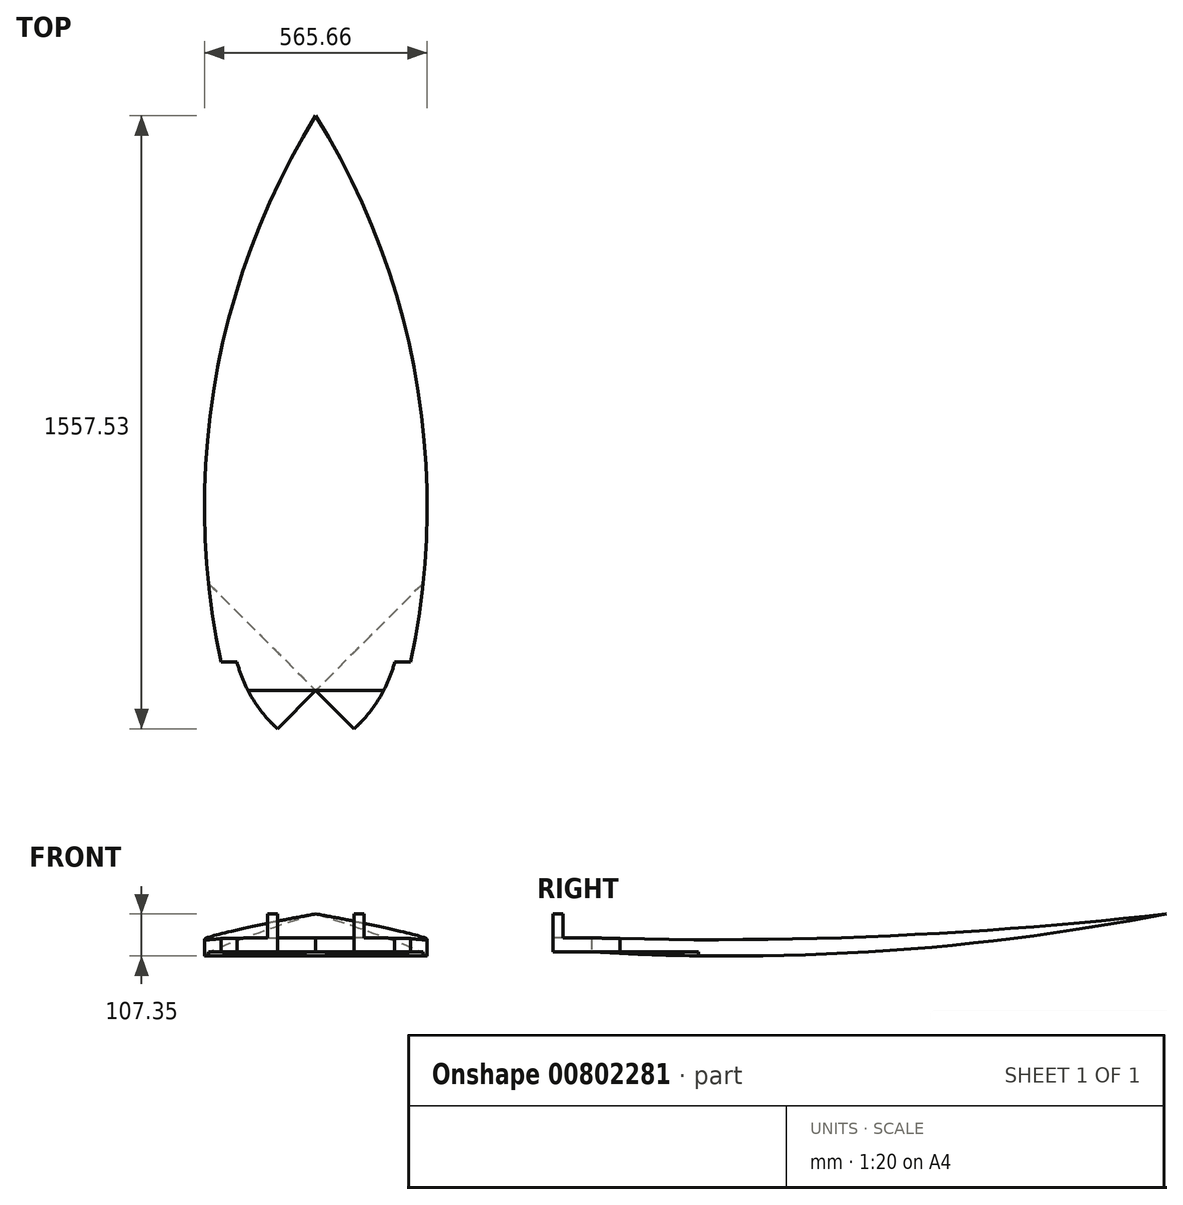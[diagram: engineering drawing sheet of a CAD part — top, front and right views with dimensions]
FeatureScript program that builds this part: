
annotation { "Feature Type Name" : "Feature", "Feature Type Description" : "" }
export const myFeature = defineFeature(function(context is Context, id is Id, definition is map)
    precondition{}
    {
        {
            var Q0;
            Q0=qCreatedBy(makeId("Top.planeOp"),FACE);
            var sketch = newSketch(context, id + "F0", { "sketchPlane" : qUnion([Q0])});
            skLineSegment(sketch, "E0", {"start": v(0, 97.23) * mm, "end": v(0, 1557.53) * mm});
            skArc(sketch, "E1", {"start": v(240.8, 169.76) * mm, "mid": v(255.12, 887.02) * mm, "end": v(0, 1557.53) * mm});
            skLineSegment(sketch, "E2", {"start": v(240.8, 169.76) * mm, "end": v(200.23, 169.76) * mm});
            skArc(sketch, "E3", {"start": v(97.15, 0) * mm, "mid": v(161.15, 77.32) * mm, "end": v(200.23, 169.76) * mm});
            skLineSegment(sketch, "E4", {"start": v(97.15, 0) * mm, "end": v(0, 97.23) * mm});
            skSolve(sketch);
        }
        {
            var Q0;
            Q0=makeQuery(id+"F0.imprint","IMPRINT",FACE,{"disambiguationData":[TD([[makeQuery(id+"F0.imprint","IMPRINT",EDGE,{"derivedFrom":sQuery(id+"F0.wireOp",EDGE,"E0")}),-1.0]])]});
            extrude(context, id + "F1", {"entities" : qUnion([Q0]), "depth" : 121.92 * mm, "offsetDistance" : 30.48 * mm});
        }
        {
            var Q0;
            Q0=makeQuery(id+"F1.opExtrude","SWEPT_FACE",FACE,{"disambiguationData":[OSD([sQuery(id+"F0.wireOp",EDGE,"E0")])]});
            var sketch = newSketch(context, id + "F2", { "sketchPlane" : qUnion([Q0])});
            skArc(sketch, "E5", {"start": v(-1557.53, 121.92) * mm, "mid": v(-828.48, 64.93) * mm, "end": v(-97.23, 60.96) * mm});
            skArc(sketch, "E6", {"start": v(-1557.53, 121.92) * mm, "mid": v(-830.46, 27.02) * mm, "end": v(-97.23, 25.6) * mm});
            skSolve(sketch);
        }
        {
            var Q0;
            {var subQ0=sQuery(id+"F2.wireOp",EDGE,"E5");Q0=makeQuery(id+"F2.imprint","IMPRINT",FACE,{"disambiguationData":[TD([[makeQuery(id+"F2.imprint","IMPRINT",EDGE,{"derivedFrom":subQ0}),1.0]])]});}
            var Q1;
            {var subQ0=sQuery(id+"F2.wireOp",EDGE,"E6");Q1=makeQuery(id+"F2.imprint","IMPRINT",FACE,{"disambiguationData":[TD([[makeQuery(id+"F2.imprint","IMPRINT",EDGE,{"derivedFrom":subQ0}),-1.0]])]});}
            extrude(context, id + "F3", {"entities" : qUnion([Q0, Q1]), "operationType" : NewBodyOperationType.REMOVE, "endBound" : BoundingType.THROUGH_ALL, "oppositeDirection" : true, "depth" : 30.48 * mm, "offsetDistance" : 30.48 * mm});
        }
        {
            var Q0;
            Q0=makeQuery(id+"F1.opExtrude","SWEPT_FACE",FACE,{"disambiguationData":[OSD([sQuery(id+"F0.wireOp",EDGE,"E4")])]});
            var sketch = newSketch(context, id + "F4", { "sketchPlane" : qUnion([Q0])});
            skLineSegment(sketch, "E7", {"start": v(-68.77, 60.96) * mm, "end": v(68.67, 60.96) * mm});
            skLineSegment(sketch, "E8", {"start": v(-68.77, 25.6) * mm, "end": v(68.67, 25.6) * mm});
            skSolve(sketch);
        }
        {
            var Q0;
            Q0 = qSketchRegion(id + "F4", true);
            var Q1;
            {var subQ0=sQuery(id+"F4.wireOp",EDGE,"E7");Q1=makeQuery(id+"F4.imprint","IMPRINT",FACE,{"disambiguationData":[TD([[makeQuery(id+"F4.imprint","IMPRINT",EDGE,{"derivedFrom":subQ0}),1.0]])]});}
            var Q2;
            {var subQ0=sQuery(id+"F4.wireOp",EDGE,"E8");Q2=makeQuery(id+"F4.imprint","IMPRINT",FACE,{"disambiguationData":[TD([[makeQuery(id+"F4.imprint","IMPRINT",EDGE,{"derivedFrom":subQ0}),-1.0]])]});}
            extrude(context, id + "F5", {"entities" : qUnion([Q0, Q1, Q2]), "operationType" : NewBodyOperationType.REMOVE, "endBound" : BoundingType.THROUGH_ALL, "oppositeDirection" : true, "depth" : 30.48 * mm, "offsetDistance" : 30.48 * mm});
        }
        {
            var Q0;
            {var subQ0=sQuery(id+"F0.wireOp",EDGE,"E4");var subQ1=sQuery(id+"F0.wireOp",EDGE,"E3");var subQ2=makeQuery(id+"F1.opExtrude","SWEPT_EDGE",EDGE,{"disambiguationData":[OSD([subQ1,subQ0])]});Q0=makeQuery(id+"F5.boolean.opBoolean","COPY",FACE,{"derivedFrom":makeQuery(id+"F5.opExtrude","SWEPT_FACE",FACE,{"disambiguationData":[OSD([subQ1,subQ0]),TDD([makeQuery(id+"F4.imprint","IMPRINT",EDGE,{"disambiguationData":[TD([[makeQuery(id+"F4.imprint","INTERSECT",VERTEX,{"derivedFrom":[subQ2,makeQuery(id+"F1.opExtrude","CAP_EDGE",EDGE,{"disambiguationData":[OSD([subQ0])],"isStart":false})]}),-1.0]])],"derivedFrom":subQ2})])]})});}
            var sketch = newSketch(context, id + "F6", { "sketchPlane" : qUnion([Q0])});
            skSolve(sketch);
        }
        {
            var Q0;
            Q0 = qSketchRegion(id + "F6", true);
            var Q1;
            {var subQ0=sQuery(id+"F0.wireOp",EDGE,"E4");var subQ1=sQuery(id+"F0.wireOp",EDGE,"E3");var subQ2=makeQuery(id+"F1.opExtrude","SWEPT_EDGE",EDGE,{"disambiguationData":[OSD([subQ1,subQ0])]});var subQ3=makeQuery(id+"F4.imprint","INTERSECT",VERTEX,{"derivedFrom":[subQ2,makeQuery(id+"F1.opExtrude","CAP_EDGE",EDGE,{"disambiguationData":[OSD([subQ0])],"isStart":false})]});Q1=makeQuery(id+"F6.imprint","IMPRINT",FACE,{"disambiguationData":[TD([[makeQuery(id+"F6.imprint","IMPRINT",EDGE,{"derivedFrom":makeQuery(id+"F5.boolean.opBoolean","COPY",EDGE,{"derivedFrom":makeQuery(id+"F5.opExtrude","SWEPT_EDGE",EDGE,{"disambiguationData":[OSD([subQ1,subQ0]),TDD([subQ3])]})})}),-1.0]])]});}
            var Q2;
            {var subQ0=sQuery(id+"F0.wireOp",EDGE,"E4");var subQ1=sQuery(id+"F0.wireOp",EDGE,"E3");var subQ2=makeQuery(id+"F1.opExtrude","SWEPT_EDGE",EDGE,{"disambiguationData":[OSD([subQ1,subQ0])]});Q2=makeQuery(id+"F5.boolean.opBoolean","COPY",FACE,{"derivedFrom":makeQuery(id+"F5.opExtrude","SWEPT_FACE",FACE,{"disambiguationData":[OSD([subQ1,subQ0]),TDD([makeQuery(id+"F4.imprint","IMPRINT",EDGE,{"disambiguationData":[TD([[makeQuery(id+"F4.imprint","INTERSECT",VERTEX,{"derivedFrom":[subQ2,makeQuery(id+"F1.opExtrude","CAP_EDGE",EDGE,{"disambiguationData":[OSD([subQ0])],"isStart":true})]}),1.0]])],"derivedFrom":subQ2})])]})});}
            extrude(context, id + "F7", {"entities" : qUnion([Q0, Q1, Q2]), "operationType" : NewBodyOperationType.REMOVE, "endBound" : BoundingType.THROUGH_ALL, "oppositeDirection" : true, "depth" : 30.48 * mm, "offsetDistance" : 30.48 * mm});
        }
        {
            var Q0;
            Q0=makeQuery(id+"F1.opExtrude","SWEPT_BODY",BODY,{"disambiguationData":[OSD([sQuery(id+"F0.wireOp",EDGE,"E0"),sQuery(id+"F0.wireOp",EDGE,"E1"),sQuery(id+"F0.wireOp",EDGE,"E2"),sQuery(id+"F0.wireOp",EDGE,"E3"),sQuery(id+"F0.wireOp",EDGE,"E4")])]});
            var Q1;
            Q1=makeQuery(id+"F1.opExtrude","SWEPT_FACE",FACE,{"disambiguationData":[OSD([sQuery(id+"F0.wireOp",EDGE,"E0")])]});
            mirror(context, id + "F8", {"operationType" : NewBodyOperationType.ADD, "entities" : qUnion([Q0]), "mirrorPlane" : qUnion([Q1])});
        }
    });
